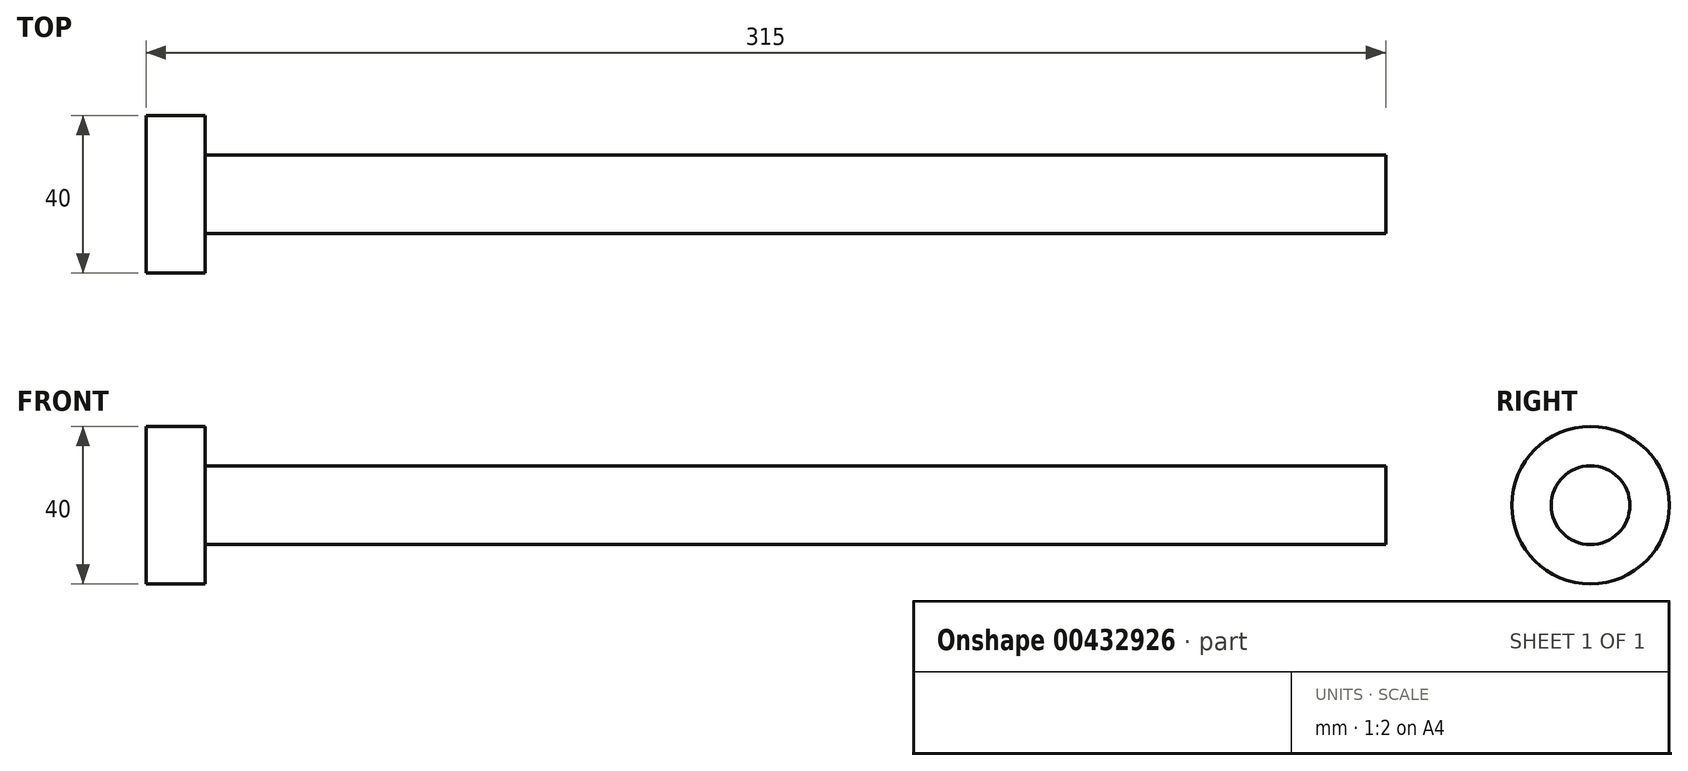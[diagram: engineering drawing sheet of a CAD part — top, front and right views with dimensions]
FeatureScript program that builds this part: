
annotation { "Feature Type Name" : "Feature", "Feature Type Description" : "" }
export const myFeature = defineFeature(function(context is Context, id is Id, definition is map)
    precondition{}
    {
        {
            var Q0;
            Q0=qCreatedBy(makeId("Right.planeOp"),FACE);
            var sketch = newSketch(context, id + "F0", { "sketchPlane" : qUnion([Q0])});
            skCircle(sketch, "E0", {"center": v(0, 0) * mm, "radius": 10 * mm});
            skSolve(sketch);
        }
        {
            var Q0;
            Q0=makeQuery(id+"F0.imprint","IMPRINT",FACE,{"disambiguationData":[TD([[makeQuery(id+"F0.imprint","IMPRINT",EDGE,{"derivedFrom":sQuery(id+"F0.wireOp",EDGE,"E0")}),1.0]])]});
            extrude(context, id + "F1", {"entities" : qUnion([Q0]), "depth" : 300 * mm});
        }
        {
            var Q0;
            Q0=qCreatedBy(makeId("Right.planeOp"),FACE);
            var sketch = newSketch(context, id + "F2", { "sketchPlane" : qUnion([Q0])});
            skCircle(sketch, "E1", {"center": v(0, 0) * mm, "radius": 20 * mm});
            skSolve(sketch);
        }
        {
            var Q0;
            Q0=makeQuery(id+"F2.imprint","IMPRINT",FACE,{"disambiguationData":[TD([[makeQuery(id+"F2.imprint","IMPRINT",EDGE,{"derivedFrom":sQuery(id+"F2.wireOp",EDGE,"E1")}),1.0]])]});
            extrude(context, id + "F3", {"entities" : qUnion([Q0]), "operationType" : NewBodyOperationType.ADD, "depth" : -15 * mm});
        }
    });
